# Revit family: Lighting-UrbanSystem-GEWISS-URBAN[O3]-LED-BRACKETSGW_OPTIC_CYCLE-PEDESTRIAN
name_source: partatom
category: Apparecchi per illuminazione
units: mm (PartAtom-declared; Revit-internal decimal feet)

## family parameters
Condiviso = No
Host = Superficie
Numero OmniClass = 23.80.70.00
Punto di calcolo locali = Sì
Quota connettore circolare = Usa diametro
Sorgente d'illuminazione = No
Taglio con vuoti quando caricato = No
Tipo di parte = Normale
Titolo OmniClass = Lighting

## types (3) — shared parameters
Application = External
Catalogue = LIGHTING
Catalogue Range = URBAN [O3]
Colour = Midnight blue
Colour temperature = 3500 K (CRI 85)
Colour temperature: = 3500 K (CRI 85)
Driver type = Constant Current Driver Led
Electrocod = 244C
Finitura = GEWISS - BLU NOTTE
IDF = d6815caf-acd5-46d1-9e92-836335ee2de2
IDT = a19afcb9-5bbe-476a-b188-1c900bde322b
IP degree = IP66
Immagine tipo = GW87908.jpg
Insulation class = II
LED Life time (L80B10) = 100000H
LED Life time (L90B20) = 50000H
LED LifeTime (L80B20) = 50000H
LED current = 530mA
Maximum surface exposed to the wind = 0,25M2
Minimum distance from the illuminated object = 1M
Operating temperature: = -25 +35 °C
Optic = Cycle and pedestrian - ULOR: 0%
Photobiologic Risk = RG1/RG2 @ 20cm
Pilot current = 530mA
Produttore = GEWISS S.p.A.
Prospetto di default = 1219 mm
Risk photobiological = RG1/RG2 @ 20cm
SEO = Street lighting
Shock resistance = IK08 BODY - IK06 LENS
Suitable for = Gewiss side brackets
Suitable for: = Gewiss side brackets
Technical sheet = https://www.gewiss.com
Type of lamp: = LED
Type of light source = LED
URL = https://www.gewiss.com
Version file RFA = 20.11
Vetro = GEWISS - VETRO
Voltage = 220/240 V - 50/60 Hz - Stand alone and/or possibility of dimmer 1-10 V
Voltage: = 220/240 V - 50/60 Hz
Warranty = 5 years
Working temperature = -25 +35 °C

## per-type parameters (varying)
| type | Descrizione | EAN code | Lumen output (lm) | Modello | No. Chorus modules | Nominal flux (lm) | Number of modules | System power | Weight (kg) | Weight (kg): |
| GWS7503B - URBAN 4 MOD.LED 3500K CYCL.OPT.BLUE | URBAN 4 MOD.LED 3500K CYCL.OPT.BLUE | 8011564868953 | 6210 | GWS7503B | 4 (4x16 LED) | 7540 | 4 (4x16 LED) | 105W | 9,5 | 9,5 |
| GWS7501B - URBAN 2 MOD.LED 3500K CYCL.OPT.BLUE | URBAN 2 MOD.LED 3500K CYCL.OPT.BLUE | 8011564868939 | 3240 | GWS7501B | 2 (2x16 LED) | 3940 | 2 (2x16 LED) | 54W | 8,2 | 8,2 |
| GWS7502B - URBAN 3 MOD.LED 3500K CYCL.OPT.GR.BLUE | URBAN 3 MOD.LED 3500K CYCL.OPT.GR.BLUE | 8011564868946 | 4740 | GWS7502B | 3 (3x16 LED) | 5760 | 3 (3x16 LED) | 81W | 8,8 | 8,8 |

## geometry (parser evidence)
native form markers: Blend x4
no freeform markers — native parametric forms only
